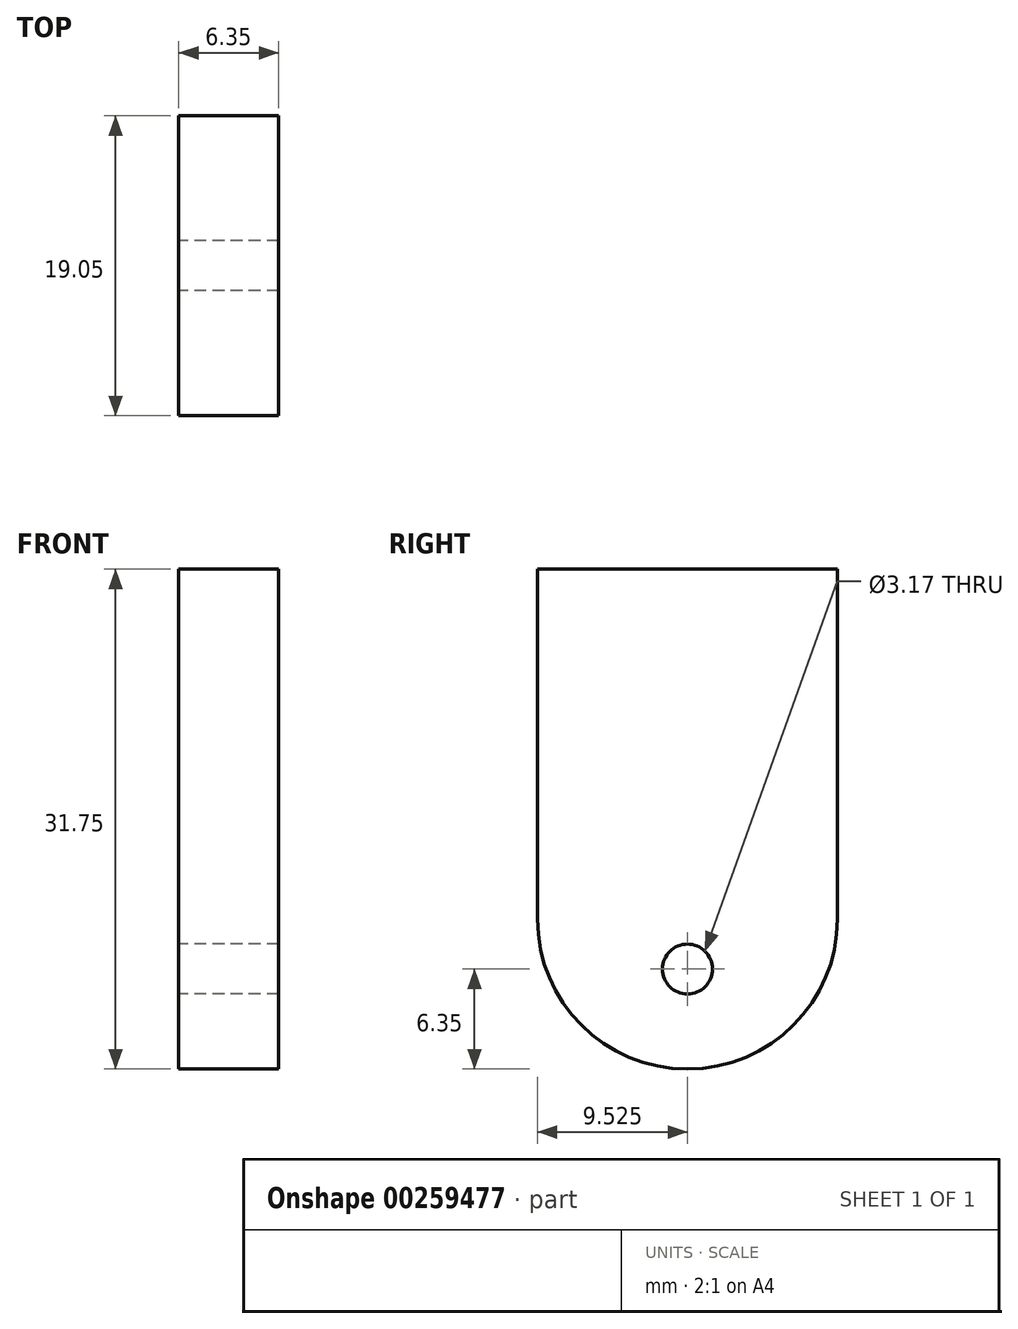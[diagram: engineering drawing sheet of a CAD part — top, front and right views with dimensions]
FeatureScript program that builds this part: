
annotation { "Feature Type Name" : "Feature", "Feature Type Description" : "" }
export const myFeature = defineFeature(function(context is Context, id is Id, definition is map)
    precondition{}
    {
        {
            var Q0;
            Q0=qCreatedBy(makeId("Right.planeOp"),FACE);
            var sketch = newSketch(context, id + "F0", { "sketchPlane" : qUnion([Q0])});
            skLineSegment(sketch, "E0", {"start": v(0, -22.23) * mm, "end": v(0, 0) * mm});
            skLineSegment(sketch, "E1", {"start": v(0, 0) * mm, "end": v(19.05, 0) * mm});
            skLineSegment(sketch, "E2", {"start": v(19.05, 0) * mm, "end": v(19.05, -22.23) * mm});
            skArc(sketch, "E3", {"start": v(0, -22.23) * mm, "mid": v(9.52, -31.75) * mm, "end": v(19.05, -22.23) * mm});
            skCircle(sketch, "E4", {"center": v(9.53, -25.4) * mm, "radius": 1.59 * mm});
            skSolve(sketch);
        }
        {
            var Q0;
            Q0=makeQuery(id+"F0.imprint","IMPRINT",FACE,{"disambiguationData":[TD([[makeQuery(id+"F0.imprint","IMPRINT",EDGE,{"derivedFrom":sQuery(id+"F0.wireOp",EDGE,"E0")}),-1.0]])]});
            extrude(context, id + "F1", {"entities" : qUnion([Q0]), "depth" : 6.35 * mm});
        }
    });
